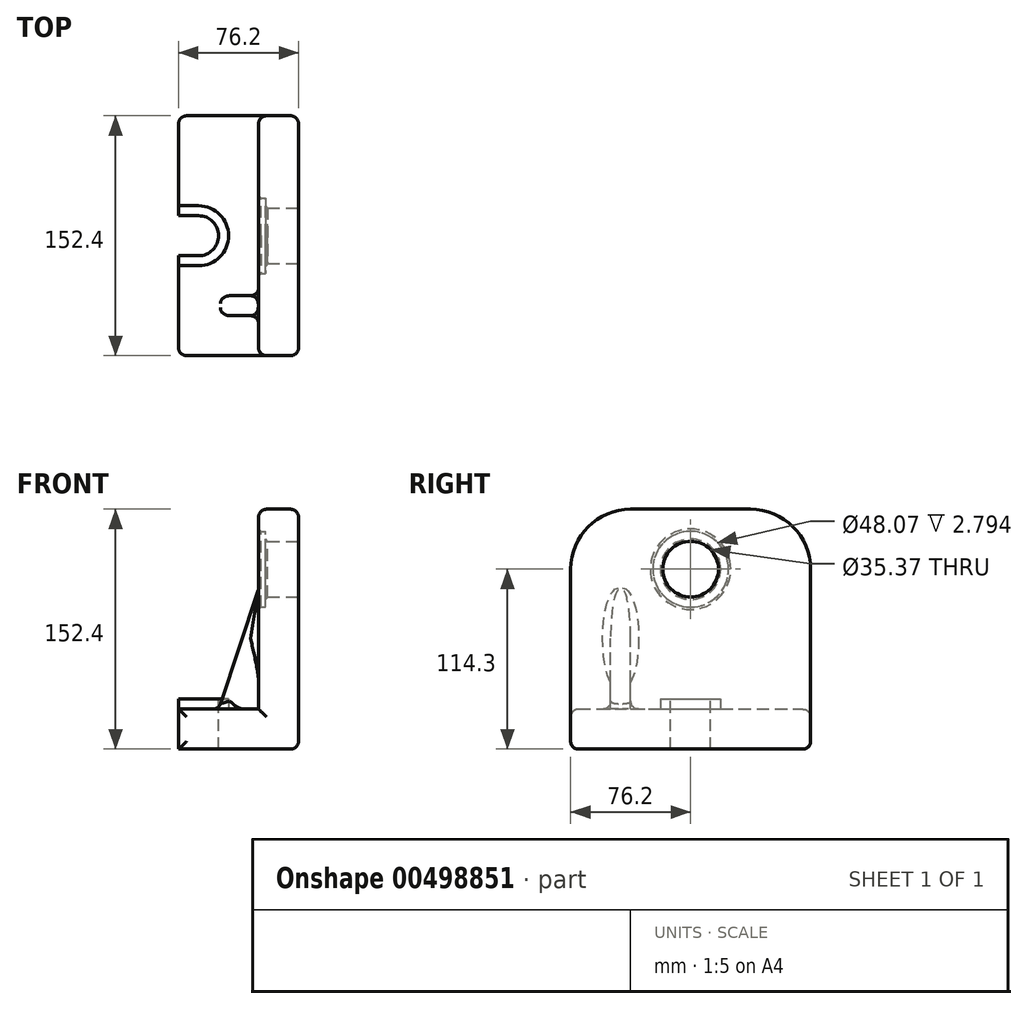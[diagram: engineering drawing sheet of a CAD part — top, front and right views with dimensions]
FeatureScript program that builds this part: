
annotation { "Feature Type Name" : "Feature", "Feature Type Description" : "" }
export const myFeature = defineFeature(function(context is Context, id is Id, definition is map)
    precondition{}
    {
        {
            var Q0;
            Q0=qCreatedBy(makeId("Front.planeOp"),FACE);
            var sketch = newSketch(context, id + "F0", { "sketchPlane" : qUnion([Q0])});
            skLineSegment(sketch, "E0", {"start": v(0, 0) * mm, "end": v(0, 152.4) * mm});
            skLineSegment(sketch, "E1", {"start": v(0, 152.4) * mm, "end": v(-25.4, 152.4) * mm});
            skLineSegment(sketch, "E2", {"start": v(-25.4, 25.4) * mm, "end": v(-25.4, 152.4) * mm});
            skLineSegment(sketch, "E3", {"start": v(0, 0) * mm, "end": v(-76.2, 0) * mm});
            skLineSegment(sketch, "E4", {"start": v(-76.2, 0) * mm, "end": v(-76.2, 25.4) * mm});
            skLineSegment(sketch, "E5", {"start": v(-76.2, 25.4) * mm, "end": v(-25.4, 25.4) * mm});
            skSolve(sketch);
        }
        {
            var Q0;
            Q0=makeQuery(id+"F0.imprint","IMPRINT",FACE,{"disambiguationData":[TD([[makeQuery(id+"F0.imprint","IMPRINT",EDGE,{"derivedFrom":sQuery(id+"F0.wireOp",EDGE,"E0")}),1.0]])]});
            extrude(context, id + "F1", {"entities" : qUnion([Q0]), "endBound" : BoundingType.SYMMETRIC, "depth" : 152.4 * mm, "offsetDistance" : 25.4 * mm});
        }
        {
            var Q0;
            Q0=makeQuery(id+"F1.opExtrude","SWEPT_FACE",FACE,{"disambiguationData":[OSD([sQuery(id+"F0.wireOp",EDGE,"E0")])]});
            var sketch = newSketch(context, id + "F2", { "sketchPlane" : qUnion([Q0])});
            skCircle(sketch, "E6", {"center": v(0, 114.3) * mm, "radius": 24.03 * mm});
            skSolve(sketch);
        }
        {
            var Q0;
            Q0=makeQuery(id+"F2.imprint","IMPRINT",FACE,{"disambiguationData":[TD([[makeQuery(id+"F2.imprint","IMPRINT",EDGE,{"derivedFrom":sQuery(id+"F2.wireOp",EDGE,"E6")}),1.0]])]});
            extrude(context, id + "F3", {"entities" : qUnion([Q0]), "operationType" : NewBodyOperationType.REMOVE, "endBound" : BoundingType.THROUGH_ALL, "oppositeDirection" : true, "depth" : 29.97 * mm, "offsetDistance" : 25.4 * mm});
        }
        {
            var Q0;
            Q0=makeQuery(id+"F1.opExtrude","SWEPT_FACE",FACE,{"disambiguationData":[OSD([sQuery(id+"F0.wireOp",EDGE,"E5")])]});
            var sketch = newSketch(context, id + "F4", { "sketchPlane" : qUnion([Q0])});
            skLineSegment(sketch, "E7", {"start": v(-76.2, 12.7) * mm, "end": v(-63.5, 12.7) * mm});
            skArc(sketch, "E8", {"start": v(-63.5, 12.7) * mm, "mid": v(-50.8, 0) * mm, "end": v(-63.5, -12.7) * mm});
            skLineSegment(sketch, "E9", {"start": v(-63.5, -12.7) * mm, "end": v(-76.2, -12.7) * mm});
            skSolve(sketch);
        }
        {
            var Q0;
            {var subQ0=sQuery(id+"F4.wireOp",EDGE,"E7");Q0=makeQuery(id+"F4.imprint","IMPRINT",FACE,{"disambiguationData":[TD([[makeQuery(id+"F4.imprint","IMPRINT",EDGE,{"derivedFrom":subQ0}),-1.0]])]});}
            extrude(context, id + "F5", {"entities" : qUnion([Q0]), "operationType" : NewBodyOperationType.REMOVE, "endBound" : BoundingType.THROUGH_ALL, "oppositeDirection" : true, "depth" : 25.4 * mm, "offsetDistance" : 25.4 * mm});
        }
        {
            var Q0;
            Q0=makeQuery(id+"F1.opExtrude","SWEPT_FACE",FACE,{"disambiguationData":[OSD([sQuery(id+"F0.wireOp",EDGE,"E2")])]});
            var sketch = newSketch(context, id + "F6", { "sketchPlane" : qUnion([Q0])});
            skLineSegment(sketch, "E10.0", {"start": v(-76.2, 25.4) * mm, "end": v(-76.2, 152.4) * mm});
            skLineSegment(sketch, "E10.1", {"start": v(76.2, 152.4) * mm, "end": v(-76.2, 152.4) * mm});
            skLineSegment(sketch, "E10.2", {"start": v(76.2, 25.4) * mm, "end": v(76.2, 152.4) * mm});
            skCircle(sketch, "E11", {"center": v(-38.1, 114.3) * mm, "radius": 38.1 * mm});
            skCircle(sketch, "E12.MirrorC", {"center": v(38.1, 114.3) * mm, "radius": 38.1 * mm});
            skSolve(sketch);
        }
        {
            var Q0;
            {var subQ0=sQuery(id+"F6.wireOp",EDGE,"E10.1");var subQ1=sQuery(id+"F6.wireOp",EDGE,"E10.0");var subQ2=makeQuery(id+"F6.imprint","INTERSECT",VERTEX,{"derivedFrom":[subQ1,subQ0]});Q0=makeQuery(id+"F6.imprint","IMPRINT",FACE,{"disambiguationData":[TD([[makeQuery(id+"F6.imprint","IMPRINT",EDGE,{"disambiguationData":[TD([[subQ2,1.0]])],"derivedFrom":subQ1}),-1.0]])]});}
            extrude(context, id + "F7", {"entities" : qUnion([Q0]), "operationType" : NewBodyOperationType.REMOVE, "endBound" : BoundingType.THROUGH_ALL, "oppositeDirection" : true, "depth" : 25.4 * mm, "offsetDistance" : 25.4 * mm});
        }
        {
            var Q0;
            {var subQ0=sQuery(id+"F6.wireOp",EDGE,"E10.2");var subQ1=sQuery(id+"F6.wireOp",EDGE,"E10.1");var subQ2=makeQuery(id+"F6.imprint","INTERSECT",VERTEX,{"derivedFrom":[subQ1,subQ0]});Q0=makeQuery(id+"F6.imprint","IMPRINT",FACE,{"disambiguationData":[TD([[makeQuery(id+"F6.imprint","IMPRINT",EDGE,{"disambiguationData":[TD([[subQ2,-1.0]])],"derivedFrom":subQ1}),1.0]])]});}
            extrude(context, id + "F8", {"entities" : qUnion([Q0]), "operationType" : NewBodyOperationType.REMOVE, "endBound" : BoundingType.THROUGH_ALL, "oppositeDirection" : true, "depth" : 25.4 * mm, "offsetDistance" : 25.4 * mm});
        }
        {
            var Q0;
            Q0=makeQuery(id+"F1.opExtrude","SWEPT_FACE",FACE,{"disambiguationData":[OSD([sQuery(id+"F0.wireOp",EDGE,"E0")])]});
            var sketch = newSketch(context, id + "F9", { "sketchPlane" : qUnion([Q0])});
            skCircle(sketch, "E13", {"center": v(0, 114.3) * mm, "radius": 17.68 * mm});
            skSolve(sketch);
        }
        {
            var Q0;
            Q0=makeQuery(id+"F9.imprint","IMPRINT",FACE,{"disambiguationData":[TD([[makeQuery(id+"F9.imprint","IMPRINT",EDGE,{"derivedFrom":sQuery(id+"F9.wireOp",EDGE,"E13")}),-1.0]])]});
            extrude(context, id + "F10", {"entities" : qUnion([Q0]), "operationType" : NewBodyOperationType.ADD, "oppositeDirection" : true, "depth" : 21.08 * mm, "offsetDistance" : 25.4 * mm});
        }
        {
            var Q0;
            Q0=qCreatedBy(makeId("Front.planeOp"),FACE);
            cPlane(context, id + "F11", {"entities" : qUnion([Q0]), "cplaneType" : CPlaneType.OFFSET, "offset" : 44.45 * mm, "width" : 152.4 * mm, "height" : 152.4 * mm});
        }
        {
            var Q0;
            Q0=qCreatedBy(id+"F11.planeOp",FACE);
            var sketch = newSketch(context, id + "F12", { "sketchPlane" : qUnion([Q0])});
            skLineSegment(sketch, "E14.0", {"start": v(-25.4, 25.4) * mm, "end": v(-25.4, 101.6) * mm});
            skLineSegment(sketch, "E14.1", {"start": v(-50.8, 25.4) * mm, "end": v(-25.4, 25.4) * mm});
            skLineSegment(sketch, "E15", {"start": v(-50.8, 25.4) * mm, "end": v(-25.4, 101.6) * mm});
            skLineSegment(sketch, "E16", {"start": v(-25.4, 101.6) * mm, "end": v(-25.4, 25.4) * mm});
            skPoint(sketch, "E17.orphan", {"position": v(-76.2, 25.4) * mm});
            skPoint(sketch, "E18.orphan", {"position": v(-25.4, 114.3) * mm});
            skSolve(sketch);
        }
        {
            var Q0;
            Q0=makeQuery(id+"F12.imprint","IMPRINT",FACE,{"disambiguationData":[TD([[makeQuery(id+"F12.imprint","IMPRINT",EDGE,{"derivedFrom":sQuery(id+"F12.wireOp",EDGE,"E14.1")}),1.0]])]});
            extrude(context, id + "F13", {"entities" : qUnion([Q0]), "operationType" : NewBodyOperationType.ADD, "endBound" : BoundingType.SYMMETRIC, "depth" : 12.7 * mm, "offsetDistance" : 25.4 * mm});
        }
        {
            var Q0;
            Q0=makeQuery(id+"F3.boolean.opBoolean","INTERSECT",EDGE,{"derivedFrom":[makeQuery(id+"F1.opExtrude","SWEPT_FACE",FACE,{"disambiguationData":[OSD([sQuery(id+"F0.wireOp",EDGE,"E2")])]}),makeQuery(id+"F3.opExtrude","SWEPT_FACE",FACE,{"disambiguationData":[OSD([sQuery(id+"F2.wireOp",EDGE,"E6")])]})]});
            var Q1;
            Q1=makeQuery(id+"F10.opExtrude","CAP_EDGE",EDGE,{"disambiguationData":[OSD([sQuery(id+"F9.wireOp",EDGE,"E13")])],"isStart":false});
            chamfer(context, id + "F14", {"entities" : qUnion([Q0, Q1]), "width" : 1.52 * mm, "tangentPropagation" : true});
        }
        {
            var Q0;
            Q0=makeQuery(id+"F1.opExtrude","SWEPT_FACE",FACE,{"disambiguationData":[OSD([sQuery(id+"F0.wireOp",EDGE,"E5")])]});
            var sketch = newSketch(context, id + "F15", { "sketchPlane" : qUnion([Q0])});
            skLineSegment(sketch, "E19.0", {"start": v(-76.2, 12.7) * mm, "end": v(-63.5, 12.7) * mm});
            skArc(sketch, "E19.1", {"start": v(-63.5, 12.7) * mm, "mid": v(-50.8, 0) * mm, "end": v(-63.5, -12.7) * mm});
            skLineSegment(sketch, "E19.2", {"start": v(-63.5, -12.7) * mm, "end": v(-76.2, -12.7) * mm});
            skLineSegment(sketch, "E19.3", {"start": v(-76.2, -76.2) * mm, "end": v(-76.2, -12.7) * mm});
            skLineSegment(sketch, "E19.4", {"start": v(-76.2, 12.7) * mm, "end": v(-76.2, 76.2) * mm});
            skLineSegment(sketch, "E20.0", {"start": v(-63.5, -19.05) * mm, "end": v(-76.2, -19.05) * mm});
            skArc(sketch, "E20.1", {"start": v(-63.5, 19.05) * mm, "mid": v(-44.45, 0) * mm, "end": v(-63.5, -19.05) * mm});
            skLineSegment(sketch, "E20.2", {"start": v(-76.2, 19.05) * mm, "end": v(-63.5, 19.05) * mm});
            skSolve(sketch);
        }
        {
            var Q0;
            {var subQ3=sQuery(id+"F15.wireOp",EDGE,"E19.0");Q0=makeQuery(id+"F15.imprint","IMPRINT",FACE,{"disambiguationData":[TD([[makeQuery(id+"F15.imprint","IMPRINT",EDGE,{"derivedFrom":subQ3}),1.0]])]});}
            extrude(context, id + "F16", {"entities" : qUnion([Q0]), "operationType" : NewBodyOperationType.ADD, "depth" : 6.35 * mm, "offsetDistance" : 25.4 * mm});
        }
        {
            var Q0;
            Q0=makeQuery(id+"F1.opExtrude","CAP_EDGE",EDGE,{"disambiguationData":[OSD([sQuery(id+"F0.wireOp",EDGE,"E5")])],"isStart":false});
            var Q1;
            Q1=makeQuery(id+"F1.opExtrude","CAP_EDGE",EDGE,{"disambiguationData":[OSD([sQuery(id+"F0.wireOp",EDGE,"E2")])],"isStart":false});
            var Q2;
            Q2=makeQuery(id+"F1.opExtrude","CAP_EDGE",EDGE,{"disambiguationData":[OSD([sQuery(id+"F0.wireOp",EDGE,"E5")])],"isStart":true});
            var Q3;
            Q3=makeQuery(id+"F1.opExtrude","CAP_EDGE",EDGE,{"disambiguationData":[OSD([sQuery(id+"F0.wireOp",EDGE,"E2")])],"isStart":true});
            var Q4;
            Q4=makeQuery(id+"F1.opExtrude","CAP_EDGE",EDGE,{"disambiguationData":[OSD([sQuery(id+"F0.wireOp",EDGE,"E4")])],"isStart":false});
            var Q5;
            Q5=makeQuery(id+"F8.boolean.opBoolean","INTERSECT",EDGE,{"derivedFrom":[makeQuery(id+"F1.opExtrude","SWEPT_FACE",FACE,{"disambiguationData":[OSD([sQuery(id+"F0.wireOp",EDGE,"E0")])]}),makeQuery(id+"F8.opExtrude","SWEPT_FACE",FACE,{"disambiguationData":[OSD([sQuery(id+"F6.wireOp",EDGE,"E12.MirrorC")])]})]});
            var Q6;
            Q6=makeQuery(id+"F1.opExtrude","CAP_EDGE",EDGE,{"disambiguationData":[OSD([sQuery(id+"F0.wireOp",EDGE,"E0")])],"isStart":false});
            var Q7;
            Q7=makeQuery(id+"F1.opExtrude","CAP_FACE",FACE,{"disambiguationData":[OSD([sQuery(id+"F0.wireOp",EDGE,"E0"),sQuery(id+"F0.wireOp",EDGE,"E1"),sQuery(id+"F0.wireOp",EDGE,"E2"),sQuery(id+"F0.wireOp",EDGE,"E3"),sQuery(id+"F0.wireOp",EDGE,"E4"),sQuery(id+"F0.wireOp",EDGE,"E5")])],"isStart":false});
            var Q8;
            Q8=makeQuery(id+"F1.opExtrude","SWEPT_EDGE",EDGE,{"disambiguationData":[OSD([sQuery(id+"F0.wireOp",EDGE,"E0"),sQuery(id+"F0.wireOp",EDGE,"E3")])]});
            var Q9;
            Q9=makeQuery(id+"F1.opExtrude","CAP_FACE",FACE,{"disambiguationData":[OSD([sQuery(id+"F0.wireOp",EDGE,"E0"),sQuery(id+"F0.wireOp",EDGE,"E1"),sQuery(id+"F0.wireOp",EDGE,"E2"),sQuery(id+"F0.wireOp",EDGE,"E3"),sQuery(id+"F0.wireOp",EDGE,"E4"),sQuery(id+"F0.wireOp",EDGE,"E5")])],"isStart":true});
            var Q10;
            Q10=makeQuery(id+"F7.boolean.opBoolean","INTERSECT",EDGE,{"derivedFrom":[makeQuery(id+"F1.opExtrude","SWEPT_FACE",FACE,{"disambiguationData":[OSD([sQuery(id+"F0.wireOp",EDGE,"E0")])]}),makeQuery(id+"F7.opExtrude","SWEPT_FACE",FACE,{"disambiguationData":[OSD([sQuery(id+"F6.wireOp",EDGE,"E11")])]})]});
            var Q11;
            Q11=makeQuery(id+"F7.boolean.opBoolean","COPY",EDGE,{"derivedFrom":makeQuery(id+"F7.opExtrude","CAP_EDGE",EDGE,{"disambiguationData":[OSD([sQuery(id+"F6.wireOp",EDGE,"E11")])],"isStart":true})});
            var Q12;
            Q12=makeQuery(id+"F1.opExtrude","SWEPT_EDGE",EDGE,{"disambiguationData":[OSD([sQuery(id+"F0.wireOp",EDGE,"E1"),sQuery(id+"F0.wireOp",EDGE,"E2")])]});
            var Q13;
            Q13=makeQuery(id+"F1.opExtrude","SWEPT_EDGE",EDGE,{"disambiguationData":[OSD([sQuery(id+"F0.wireOp",EDGE,"E0"),sQuery(id+"F0.wireOp",EDGE,"E1")])]});
            var Q14;
            Q14=makeQuery(id+"F8.boolean.opBoolean","COPY",EDGE,{"derivedFrom":makeQuery(id+"F8.opExtrude","CAP_EDGE",EDGE,{"disambiguationData":[OSD([sQuery(id+"F6.wireOp",EDGE,"E12.MirrorC")])],"isStart":true})});
            var Q15;
            Q15=makeQuery(id+"F13.opExtrude","CAP_EDGE",EDGE,{"disambiguationData":[OSD([sQuery(id+"F12.wireOp",EDGE,"E16")])],"isStart":false});
            var Q16;
            Q16=makeQuery(id+"F13.opExtrude","CAP_EDGE",EDGE,{"disambiguationData":[OSD([sQuery(id+"F12.wireOp",EDGE,"E14.1")])],"isStart":false});
            var Q17;
            Q17=makeQuery(id+"F13.opExtrude","CAP_EDGE",EDGE,{"disambiguationData":[OSD([sQuery(id+"F12.wireOp",EDGE,"E15")])],"isStart":false});
            var Q18;
            Q18=makeQuery(id+"F13.opExtrude","SWEPT_FACE",FACE,{"disambiguationData":[OSD([sQuery(id+"F12.wireOp",EDGE,"E15")])]});
            var Q19;
            Q19=makeQuery(id+"F13.opExtrude","CAP_EDGE",EDGE,{"disambiguationData":[OSD([sQuery(id+"F12.wireOp",EDGE,"E14.1")])],"isStart":true});
            var Q20;
            Q20=makeQuery(id+"F13.opExtrude","CAP_EDGE",EDGE,{"disambiguationData":[OSD([sQuery(id+"F12.wireOp",EDGE,"E16")])],"isStart":true});
            var Q21;
            Q21=makeQuery(id+"FhhevGgaAtH690c_1.1.F13.opExtrude","SWEPT_EDGE",EDGE,{"disambiguationData":[OSD([sQuery(id+"F12.wireOp",EDGE,"E15"),sQuery(id+"F12.wireOp",EDGE,"E16")])]});
            var Q22;
            Q22=makeQuery(id+"FhhevGgaAtH690c_1.1.F13.opExtrude","CAP_EDGE",EDGE,{"disambiguationData":[OSD([sQuery(id+"F12.wireOp",EDGE,"E15")])],"isStart":false});
            var Q23;
            Q23=makeQuery(id+"FhhevGgaAtH690c_1.1.F13.opExtrude","CAP_EDGE",EDGE,{"disambiguationData":[OSD([sQuery(id+"F12.wireOp",EDGE,"E14.1")])],"isStart":false});
            var Q24;
            Q24=makeQuery(id+"FhhevGgaAtH690c_1.1.F13.opExtrude","CAP_EDGE",EDGE,{"disambiguationData":[OSD([sQuery(id+"F12.wireOp",EDGE,"E16")])],"isStart":false});
            var Q25;
            Q25=makeQuery(id+"FhhevGgaAtH690c_1.1.F13.opExtrude","SWEPT_EDGE",EDGE,{"disambiguationData":[OSD([sQuery(id+"F12.wireOp",EDGE,"E14.1"),sQuery(id+"F12.wireOp",EDGE,"E15")])]});
            var Q26;
            Q26=makeQuery(id+"FhhevGgaAtH690c_1.1.F13.opExtrude","CAP_EDGE",EDGE,{"disambiguationData":[OSD([sQuery(id+"F12.wireOp",EDGE,"E14.1")])],"isStart":true});
            var Q27;
            Q27=makeQuery(id+"FhhevGgaAtH690c_1.1.F13.opExtrude","CAP_EDGE",EDGE,{"disambiguationData":[OSD([sQuery(id+"F12.wireOp",EDGE,"E16")])],"isStart":true});
            var Q28;
            Q28=makeQuery(id+"FhhevGgaAtH690c_1.1.F13.opExtrude","CAP_EDGE",EDGE,{"disambiguationData":[OSD([sQuery(id+"F12.wireOp",EDGE,"E15")])],"isStart":true});
            fillet(context, id + "F17", {"entities" : qUnion([Q0, Q1, Q2, Q3, Q4, Q5, Q6, Q7, Q8, Q9, Q10, Q11, Q12, Q13, Q14, Q15, Q16, Q17, Q18, Q19, Q20, Q21, Q22, Q23, Q24, Q25, Q26, Q27, Q28]), "radius" : 5.08 * mm, "tangentPropagation" : true, "allowEdgeOverflow" : false});
        }
    });
